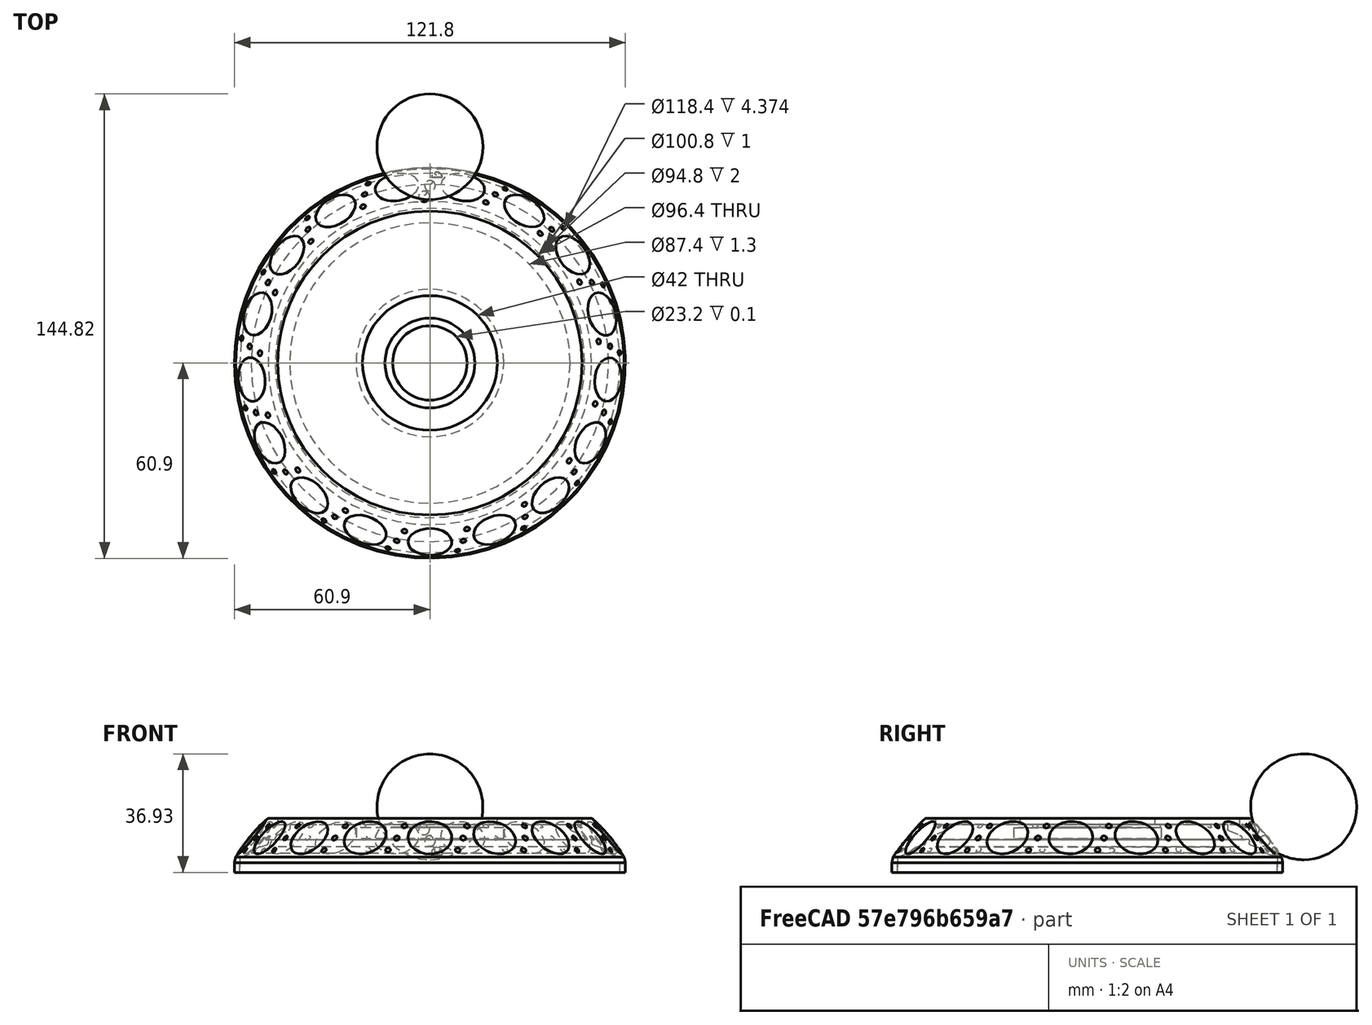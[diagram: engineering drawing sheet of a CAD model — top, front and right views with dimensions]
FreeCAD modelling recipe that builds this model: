
FCSTD DOCUMENT  (FreeCAD 0.20R29177 (Git))
Label: Stanton jog
License: All rights reserved
LicenseURL: http://en.wikipedia.org/wiki/All_rights_reserved
objects: Part::Cylinder×7, Part::Sphere×4, Part::FeaturePython×4, Part::Cut×3, Part::Fuse×3, Sketcher::SketchObject×1, Part::Revolution×1
note: 19 computed .brp shape members not serialized (recipe doc carries the construction recipe); baked Part::Feature solids carry a one-line shape summary decoded from their .brp

FEATURE [Part::Cylinder] Cylinder  label="Основа"
  Angle = 360
  AttacherType = Attacher::AttachEngine3D
  FirstAngle = 0
  Height = 4.6
  Radius = 59.2
  SecondAngle = 0
FEATURE [Part::Cylinder] Cylinder001  label="Внутренняя плоскость"
  Angle = 360
  AttacherType = Attacher::AttachEngine3D
  FirstAngle = 0
  Height = 0.05
  Placement = pos=(0,0,7.9) rot=(0,0,1;0rad)
  Radius = 47.35
  SecondAngle = 0
FEATURE [Part::Cylinder] Cylinder002  label="верхняя плоскость"
  Angle = 360
  AttacherType = Attacher::AttachEngine3D
  FirstAngle = 0
  Height = 2
  Placement = pos=(0,0,15.9) rot=(0,0,1;0rad)
  Radius = 47.4
  SecondAngle = 0
FEATURE [Part::Cylinder] Cylinder003  label="Проем для дисплея"
  Angle = 360
  AttacherType = Attacher::AttachEngine3D
  FirstAngle = 0
  Height = 2
  Placement = pos=(0,0,15.9) rot=(0,0,1;0rad)
  Radius = 21
  SecondAngle = 0
FEATURE [Part::Cut] Cut  label="Верхняя накладка"
  Base = -> Cylinder002
  Placement = pos=(0,0,-1) rot=(0,0,1;0rad)
  Tool = -> Cylinder003
FEATURE [Part::Cylinder] Cylinder004  label="Цилиндр001"
  Angle = 360
  AttacherType = Attacher::AttachEngine3D
  FirstAngle = 0
  Height = 0.1
  Radius = 14
  SecondAngle = 0
FEATURE [Part::Cylinder] Cylinder005  label="Цилиндр002"
  Angle = 360
  AttacherType = Attacher::AttachEngine3D
  FirstAngle = 0
  Height = 0.1
  Radius = 11.6
  SecondAngle = 0
FEATURE [Part::Cut] Cut001  label="Изображение на дисплее"
  Base = -> Cylinder004
  Placement = pos=(0,0,13.9) rot=(0,0,1;0rad)
  Tool = -> Cylinder005
FEATURE [Part::Cylinder] Cylinder006  label="Дисплейный модуль"
  Angle = 360
  AttacherType = Attacher::AttachEngine3D
  FirstAngle = 0
  Height = 3.45
  Placement = pos=(0,0,10.45) rot=(0,0,1;0rad)
  Radius = 23
  SecondAngle = 0
FEATURE [Sketcher::SketchObject] Sketch
  FullyConstrained = false
  Placement = pos=(0,0,0) rot=(1,0,0;1.5708rad)
  sketch-geometry (23):
    g0: LineSegment StartX=-59.2 StartY=0 StartZ=0 EndX=-60.9 EndY=0 EndZ=0
    g1: LineSegment StartX=-59.2 StartY=0 StartZ=0 EndX=-59.2 EndY=4.3742 EndZ=0
    g2: ArcOfCircle CenterX=-18.5701 CenterY=-19.9341 CenterZ=0 NormalX=0 NormalY=0 NormalZ=1 AngleXU=0 Radius=48.6815 StartAngle=2.28804 EndAngle=2.60864
    g3: LineSegment StartX=-47.4 StartY=16.9 StartZ=0 EndX=-50.1775 EndY=16.9 EndZ=0
    g4: LineSegment StartX=-47.4 StartY=16.9 StartZ=0 EndX=-47.4 EndY=14.9 EndZ=0
    g5: LineSegment StartX=-47.4 StartY=14.9 StartZ=0 EndX=-43.7 EndY=14.9 EndZ=0
    g6: LineSegment StartX=-43.7 StartY=14.9 StartZ=0 EndX=-43.7 EndY=13.6 EndZ=0
    g7: LineSegment StartX=-58.9904 StartY=4.68386 StartZ=0 EndX=-55.7 EndY=6 EndZ=0
    g8: LineSegment StartX=-48.4475 StartY=10.2 StartZ=0 EndX=-50.4 EndY=10.2 EndZ=0
    g9: LineSegment StartX=-48.2 StartY=10.4475 StartZ=0 EndX=-48.2 EndY=10.5684 EndZ=0
    g10: LineSegment StartX=-50.4 StartY=10.2 StartZ=0 EndX=-50.4 EndY=9.2 EndZ=0
    g11: LineSegment StartX=-55.7 StartY=6 StartZ=0 EndX=-54.0691 EndY=7.33434 EndZ=0
    g12: LineSegment StartX=-52.7938 StartY=8.00503 StartZ=0 EndX=-50.8802 EndY=8.56059 EndZ=0
    g13: ArcOfCircle CenterX=-51.7906 CenterY=4.54941 CenterZ=0 NormalX=0 NormalY=0 NormalZ=1 AngleXU=0 Radius=3.5983 StartAngle=1.85335 EndAngle=2.25653
    g14: ArcOfCircle CenterX=-51.0658 CenterY=9.2 CenterZ=0 NormalX=0 NormalY=0 NormalZ=1 AngleXU=0 Radius=0.665807 StartAngle=4.99494 EndAngle=6.28319
    g15: ArcOfCircle CenterX=-48.4475 CenterY=10.4475 CenterZ=0 NormalX=0 NormalY=0 NormalZ=1 AngleXU=0 Radius=0.247501 StartAngle=4.71239 EndAngle=6.28319
    g16: ArcOfCircle CenterX=-58.8665 CenterY=4.3742 CenterZ=0 NormalX=0 NormalY=0 NormalZ=1 AngleXU=0 Radius=0.333508 StartAngle=1.9513 EndAngle=3.14159
    g17: ArcOfCircle CenterX=-50.1518 CenterY=1.55596 CenterZ=0 NormalX=0 NormalY=0 NormalZ=1 AngleXU=0 Radius=10.8448 StartAngle=2.83781 EndAngle=3.00804
    g18: LineSegment StartX=-60.9 StartY=3 StartZ=0 EndX=-60.9 EndY=0 EndZ=0
    g19: LineSegment StartX=-47.526 StartY=11.5846 StartZ=0 EndX=-44.0685 EndY=13.0444 EndZ=0
    g20: ArcOfCircle CenterX=-44.3031 CenterY=13.6 CenterZ=0 NormalX=0 NormalY=0 NormalZ=1 AngleXU=0 Radius=0.603082 StartAngle=5.1119 EndAngle=6.28319
    g21: ArcOfCircle CenterX=-47.097 CenterY=10.5684 CenterZ=0 NormalX=0 NormalY=0 NormalZ=1 AngleXU=0 Radius=1.10303 StartAngle=1.97031 EndAngle=3.14159
    g22: ArcOfCircle CenterX=-50.1775 CenterY=16.3043 CenterZ=0 NormalX=0 NormalY=0 NormalZ=1 AngleXU=0 Radius=0.595692 StartAngle=1.5708 EndAngle=2.28804
  constraints (33):
    c: Horizontal(g3)
    c: Coincident(g4,g3)
    c: Vertical(g4)
    c: Coincident(g5,g4)
    c: Coincident(g6,g5)
    c: Vertical(g9)
    c: Coincident(g10,g8)
    c: Coincident(g7,g11)
    c: Tangent(g11,g13) = 1.5708
    c: Tangent(g12,g13) = 1.5708
    c: Tangent(g10,g14) = 1.5708
    c: Tangent(g12,g14) = -1.5708
    c: Tangent(g9,g15) = -1.5708
    c: Tangent(g8,g15) = 1.5708
    c: Tangent(g1,g16) = 1.5708
    c: Tangent(g7,g16) = 1.5708
    c: DistanceX(g8) = -50.4
    c: DistanceY(g8) = 10.2
    c: DistanceY(g0) = 0
    c: DistanceX(g17) = -60.9
    c: DistanceY(g17) = 3
    c: DistanceX(g2) = -60.5
    c: DistanceY(g2) = 4.8
    c: DistanceX(g3) = -47.4
    c: DistanceY(g4) = 14.9
    c: Tangent(g6,g20) = 1.5708
    c: Tangent(g19,g20) = -1.5708
    c: Tangent(g9,g21) = 1.5708
    c: Tangent(g19,g21) = 1.5708
    c: Tangent(g2,g22) = -1.5708
    c: Tangent(g3,g22) = -1.5708
    c: DistanceX(g0) = -59.2
    c: DistanceY(g0) = 0
FEATURE [Part::Sphere] Sphere  label="Сфера"
  Angle1 = -90
  Angle2 = 90
  Angle3 = 360
  AttacherType = Attacher::AttachEngine3D
  Placement = pos=(0,67.42,20.43) rot=(0,0,1;0rad)
  Radius = 16.5
FEATURE [Part::Revolution] Revolve
  Angle = 360
  Axis = (0,0,1)
  Base = (0,0,0)
  FaceMakerClass = Part::FaceMakerBullseye
  Solid = true
  Source = -> Sketch
  Symmetric = false
FEATURE [Part::FeaturePython] Array  # Draft array (typed FeaturePython)
  AlwaysSyncPlacement = false
  Angle = 360
  ArrayType = 1
  Axis = (0,0,1)
  Base = -> Sphere
  Center = (0,0,21.1)
  Count = 17
  ExpandArray = false
  Fuse = false
  IntervalAxis = (0,0,0)
  IntervalX = (50,0,0)
  IntervalY = (0,50,0)
  IntervalZ = (0,0,50)
  NumberCircles = 3
  NumberPolar = 17
  NumberX = 2
  NumberY = 2
  NumberZ = 1
  Placement = pos=(0,0,0) rot=(0,0,1;0.18483rad)
  PlacementList = 17 placements: [(0,67.42,20.43),(-24.3549,62.8673,20.43),(-45.4206,49.824,20.43),(-60.3519,30.0517,20.43),(-67.1324,6.22073,20.43),(-64.8463,-18.4504,20.43),(-53.8023,-40.6296,20.43),(-35.4921,-57.3216,20.43),(-12.3884,-66.272,20.43),(12.3884,-66.272,20.43),(35.4921,-57.3216,20.43),(53.8023,-40.6296,20.43),(64.8463,-18.4504,20.43),(67.1324,6.22073,20.43),(60.3519,30.0517,20.43),(45.4206,49.824,20.43),+1 more]
  RadialDistance = 50
  ScaleList = (17) [(1,1,1),(1,1,1),(1,1,1),(1,1,1),(1,1,1),(1,1,1),(1,1,1),(1,1,1),(1,1,1),(1,1,1),(1,1,1),(1,1,1),(1,1,1),(1,1,1),(1,1,1),(1,1,1),(1,1,1)]
  Symmetry = 1
  TangentialDistance = 25
FEATURE [Part::Cut] Cut002
  Base = -> Revolve
  Tool = -> Array
FEATURE [Part::Sphere] Sphere001  label="Сфера центральная"
  Angle1 = -90
  Angle2 = 90
  Angle3 = 360
  AttacherType = Attacher::AttachEngine3D
  Placement = pos=(0,55.29,9.8) rot=(0,0,1;0rad)
  Radius = 1.66
FEATURE [Part::Sphere] Sphere002  label="Сфера верхняя"
  Angle1 = -90
  Angle2 = 90
  Angle3 = 360
  AttacherType = Attacher::AttachEngine3D
  Placement = pos=(-1.8,51.96,13.4) rot=(0,0,1;0rad)
  Radius = 1.69
FEATURE [Part::Sphere] Sphere003  label="Сфера нижняя"
  Angle1 = -23
  Angle2 = 90
  Angle3 = 180
  AttacherType = Attacher::AttachEngine3D
  Placement = pos=(2.2,57.86,6.09) rot=(0,0,1;0rad)
  Radius = 1.71
FEATURE [Part::FeaturePython] Array001  # Draft array (typed FeaturePython)
  AlwaysSyncPlacement = false
  Angle = 360
  ArrayType = 1
  Axis = (0,0,1)
  Base = -> Sphere001
  Center = (0,0,9.8)
  Count = 17
  ExpandArray = false
  Fuse = false
  IntervalAxis = (0,0,0)
  IntervalX = (50,0,0)
  IntervalY = (0,50,0)
  IntervalZ = (0,0,50)
  NumberCircles = 3
  NumberPolar = 17
  NumberX = 2
  NumberY = 2
  NumberZ = 1
  PlacementList = 17 placements: [(0,55.29,9.8),(-19.9731,51.5564,9.8),(-37.2486,40.8598,9.8),(-49.4936,24.6449,9.8),(-55.0541,5.10152,9.8),(-53.1793,-15.1308,9.8),(-44.1224,-33.3197,9.8),(-29.1064,-47.0085,9.8),(-10.1595,-54.3486,9.8),(10.1595,-54.3486,9.8),(29.1064,-47.0085,9.8),(44.1224,-33.3197,9.8),(53.1793,-15.1308,9.8),(55.0541,5.10152,9.8),(49.4936,24.6449,9.8),(37.2486,40.8598,9.8),(19.9731,51.5564,9.8)]
  RadialDistance = 50
  ScaleList = (17) [(1,1,1),(1,1,1),(1,1,1),(1,1,1),(1,1,1),(1,1,1),(1,1,1),(1,1,1),(1,1,1),(1,1,1),(1,1,1),(1,1,1),(1,1,1),(1,1,1),(1,1,1),(1,1,1),(1,1,1)]
  Symmetry = 1
  TangentialDistance = 25
FEATURE [Part::FeaturePython] Array002  # Draft array (typed FeaturePython)
  AlwaysSyncPlacement = false
  Angle = 360
  ArrayType = 1
  Axis = (0,0,1)
  Base = -> Sphere003
  Center = (0,0,6.09)
  Count = 17
  ExpandArray = false
  Fuse = false
  IntervalAxis = (0,0,0)
  IntervalX = (50,0,0)
  IntervalY = (0,50,0)
  IntervalZ = (0,0,50)
  NumberCircles = 3
  NumberPolar = 17
  NumberX = 2
  NumberY = 2
  NumberZ = 1
  PlacementList = 17 placements: [(2.2,57.86,6.09),(-18.85,54.7476,6.09),(-37.3542,44.2412,6.09),(-50.8135,27.7598,6.09),(-57.4102,7.52926,6.09),(-56.2533,-13.7181,6.09),(-47.4991,-33.1128,6.09),(-32.3298,-48.0354,6.09),(-12.7943,-56.4706,6.09),(8.46921,-57.2791,6.09),(28.5889,-50.3517,6.09),(44.8475,-36.6241,6.09),(55.0492,-17.9502,6.09),(57.8162,3.14803,6.09),(52.7748,23.8211,6.09),(40.6058,41.2769,6.09),(22.9529,53.1581,6.09)]
  RadialDistance = 50
  ScaleList = (17) [(1,1,1),(1,1,1),(1,1,1),(1,1,1),(1,1,1),(1,1,1),(1,1,1),(1,1,1),(1,1,1),(1,1,1),(1,1,1),(1,1,1),(1,1,1),(1,1,1),(1,1,1),(1,1,1),(1,1,1)]
  Symmetry = 1
  TangentialDistance = 25
FEATURE [Part::FeaturePython] Array003  # Draft array (typed FeaturePython)
  AlwaysSyncPlacement = false
  Angle = 360
  ArrayType = 1
  Axis = (0,0,1)
  Base = -> Sphere002
  Center = (0,0,13.4)
  Count = 17
  ExpandArray = false
  Fuse = false
  IntervalAxis = (0,0,0)
  IntervalX = (50,0,0)
  IntervalY = (0,50,0)
  IntervalZ = (0,0,50)
  NumberCircles = 3
  NumberPolar = 17
  NumberX = 2
  NumberY = 2
  NumberZ = 1
  PlacementList = 17 placements: [(-1.8,51.96,13.4),(-20.4486,47.801,13.4),(-36.3354,37.1863,13.4),(-47.315,21.5493,13.4),(-51.9044,3.00194,13.4),(-49.4839,-15.9508,13.4),(-40.3802,-32.7493,13.4),(-25.823,-45.1249,13.4),(-7.77827,-51.406,13.4),(11.317,-50.7445,13.4),(28.8838,-43.2297,13.4),(42.5497,-29.8765,13.4),(50.4691,-12.4882,13.4),(51.5723,6.58659,13.4),(45.7104,24.7719,13.4),(33.675,39.6116,13.4),(17.0917,49.1015,13.4)]
  RadialDistance = 50
  ScaleList = (17) [(1,1,1),(1,1,1),(1,1,1),(1,1,1),(1,1,1),(1,1,1),(1,1,1),(1,1,1),(1,1,1),(1,1,1),(1,1,1),(1,1,1),(1,1,1),(1,1,1),(1,1,1),(1,1,1),(1,1,1)]
  Symmetry = 1
  TangentialDistance = 25
FEATURE [Part::Fuse] Fusion
  Base = -> Cut002
  Tool = -> Array001
FEATURE [Part::Fuse] Fusion001
  Base = -> Fusion
  Tool = -> Array002
FEATURE [Part::Fuse] Fusion002
  Base = -> Fusion001
  Tool = -> Array003
